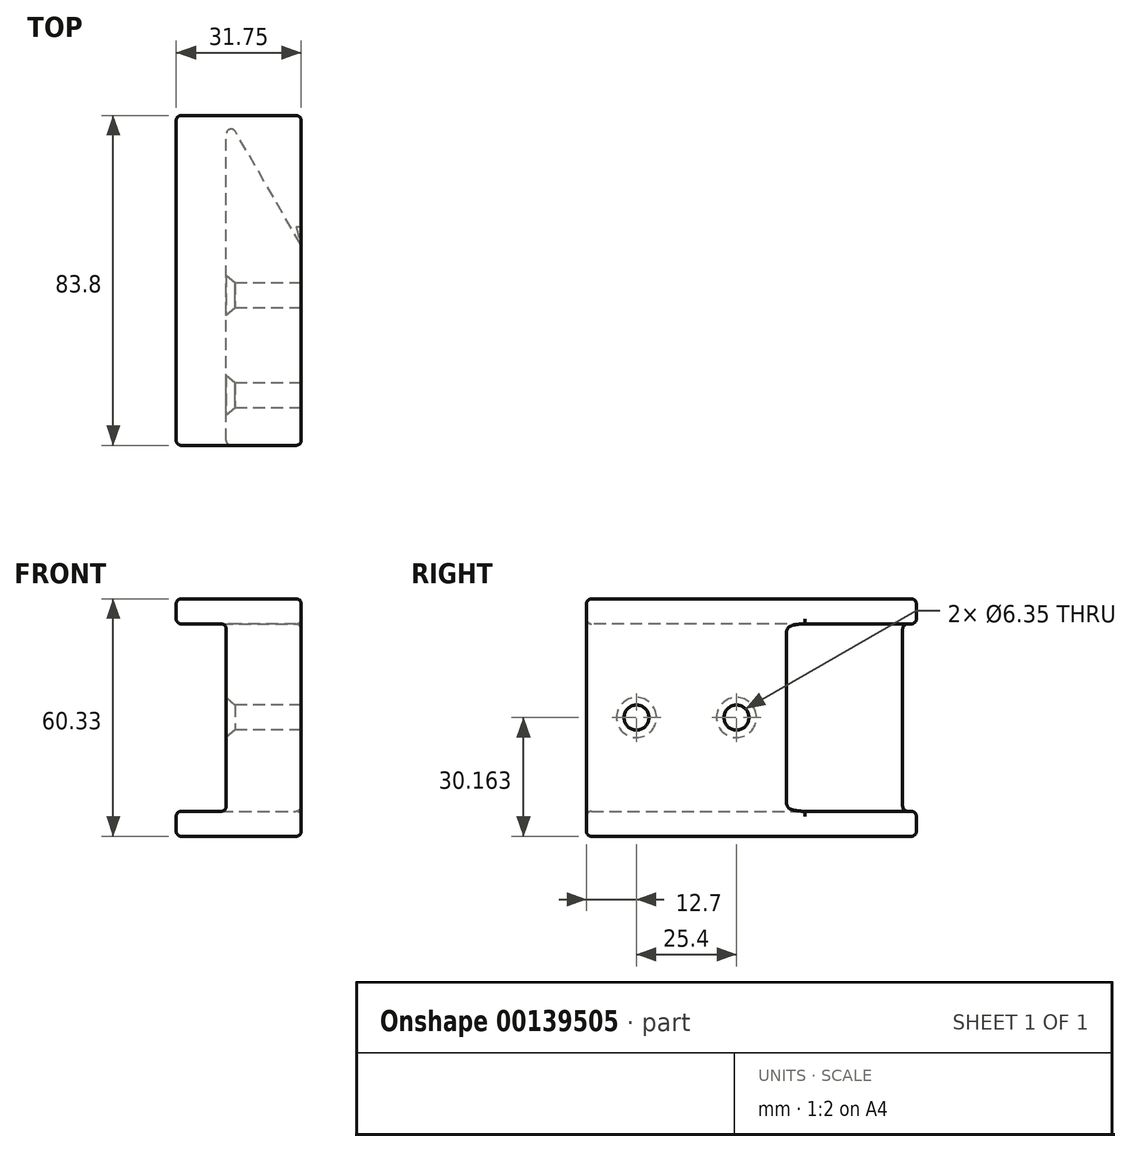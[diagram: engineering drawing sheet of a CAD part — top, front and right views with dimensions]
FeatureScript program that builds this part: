
annotation { "Feature Type Name" : "Feature", "Feature Type Description" : "" }
export const myFeature = defineFeature(function(context is Context, id is Id, definition is map)
    precondition{}
    {
        {
            var Q0;
            Q0=qCreatedBy(makeId("Top.planeOp"),FACE);
            var sketch = newSketch(context, id + "F0", { "sketchPlane" : qUnion([Q0])});
            skLineSegment(sketch, "E0", {"start": v(0, 0) * mm, "end": v(19.05, 0) * mm});
            skLineSegment(sketch, "E1", {"start": v(19.05, 0) * mm, "end": v(19.05, 50.8) * mm});
            skLineSegment(sketch, "E2", {"start": v(19.05, 50.8) * mm, "end": v(0, 83.8) * mm});
            skLineSegment(sketch, "E3", {"start": v(0, 83.8) * mm, "end": v(0, 0) * mm});
            skSolve(sketch);
        }
        {
            var Q0;
            Q0=makeQuery(id+"F0.imprint","IMPRINT",FACE,{"disambiguationData":[TD([[makeQuery(id+"F0.imprint","IMPRINT",EDGE,{"derivedFrom":sQuery(id+"F0.wireOp",EDGE,"E0")}),1.0]])]});
            extrude(context, id + "F1", {"entities" : qUnion([Q0]), "depth" : 60.32 * mm});
        }
        {
            var Q0;
            Q0=makeQuery(id+"F1.opExtrude","SWEPT_FACE",FACE,{"disambiguationData":[OSD([sQuery(id+"F0.wireOp",EDGE,"E3")])]});
            var sketch = newSketch(context, id + "F2", { "sketchPlane" : qUnion([Q0])});
            skPoint(sketch, "E4", {"position": v(-12.7, 30.16) * mm});
            skPoint(sketch, "E5", {"position": v(-38.1, 30.16) * mm});
            skLineSegment(sketch, "E6", {"start": v(-101.98, 30.16) * mm, "end": v(14.04, 30.16) * mm, "construction": true});
            skSolve(sketch);
        }
        {
            var Q0;
            Q0=sQuery(id+"F2.wireOp",VERTEX,"E4");
            var Q1;
            Q1=sQuery(id+"F2.wireOp",VERTEX,"E5");
            var Q2;
            Q2=sQuery(id+"F2.wireOp",VERTEX,"fd414b69-aa0b-4d1e-85eb-326c3dd4f586");
            var Q3;
            Q3=makeQuery(id+"F1.opExtrude","SWEPT_BODY",BODY,{"disambiguationData":[OSD([sQuery(id+"F0.wireOp",EDGE,"E0"),sQuery(id+"F0.wireOp",EDGE,"E1"),sQuery(id+"F0.wireOp",EDGE,"E2"),sQuery(id+"F0.wireOp",EDGE,"E3")])]});
            hole(context, id + "F3", {"style" : HoleStyle.C_SINK, "endStyle" : HoleEndStyle.THROUGH, "holeDiameter" : 6.35 * mm, "cSinkDiameter" : 10.16 * mm, "cSinkAngle" : 82 * degree, "startFromSketch" : true, "locations" : qUnion([Q0, Q1, Q2]), "scope" : qUnion([Q3]), "isTappedThrough" : true});
        }
        {
            var Q0;
            Q0=makeQuery(id+"F1.opExtrude","SWEPT_FACE",FACE,{"disambiguationData":[OSD([sQuery(id+"F0.wireOp",EDGE,"E1")])]});
            var sketch = newSketch(context, id + "F4", { "sketchPlane" : qUnion([Q0])});
            skLineSegment(sketch, "E7.bottom", {"start": v(83.8, 60.33) * mm, "end": v(0, 60.32) * mm});
            skLineSegment(sketch, "E7.top", {"start": v(83.8, 53.98) * mm, "end": v(0, 53.98) * mm});
            skLineSegment(sketch, "E7.left", {"start": v(83.8, 60.33) * mm, "end": v(83.8, 53.98) * mm});
            skLineSegment(sketch, "E7.right", {"start": v(0, 60.32) * mm, "end": v(0, 53.98) * mm});
            skLineSegment(sketch, "E8.bottom", {"start": v(0, 0) * mm, "end": v(83.8, 0) * mm});
            skLineSegment(sketch, "E8.top", {"start": v(0, 6.35) * mm, "end": v(83.8, 6.35) * mm});
            skLineSegment(sketch, "E8.left", {"start": v(0, 0) * mm, "end": v(0, 6.35) * mm});
            skLineSegment(sketch, "E8.right", {"start": v(83.8, 0) * mm, "end": v(83.8, 6.35) * mm});
            skSolve(sketch);
        }
        {
            var Q0;
            {var subQ3=sQuery(id+"F4.wireOp",EDGE,"E7.left");Q0=makeQuery(id+"F4.imprint","IMPRINT",FACE,{"disambiguationData":[TD([[makeQuery(id+"F4.imprint","IMPRINT",EDGE,{"derivedFrom":subQ3}),-1.0]])]});}
            var Q1;
            {var subQ3=sQuery(id+"F4.wireOp",EDGE,"E8.right");Q1=makeQuery(id+"F4.imprint","IMPRINT",FACE,{"disambiguationData":[TD([[makeQuery(id+"F4.imprint","IMPRINT",EDGE,{"derivedFrom":subQ3}),1.0]])]});}
            var Q2;
            {var subQ0=sQuery(id+"F4.wireOp",EDGE,"E7.right");Q2=makeQuery(id+"F4.imprint","IMPRINT",FACE,{"disambiguationData":[TD([[makeQuery(id+"F4.imprint","IMPRINT",EDGE,{"derivedFrom":subQ0}),1.0]])]});}
            var Q3;
            {var subQ0=sQuery(id+"F4.wireOp",EDGE,"E8.left");Q3=makeQuery(id+"F4.imprint","IMPRINT",FACE,{"disambiguationData":[TD([[makeQuery(id+"F4.imprint","IMPRINT",EDGE,{"derivedFrom":subQ0}),1.0]])]});}
            extrude(context, id + "F5", {"entities" : qUnion([Q0, Q1, Q2, Q3]), "operationType" : NewBodyOperationType.ADD, "oppositeDirection" : true, "depth" : 31.75 * mm});
        }
        {
            var Q0;
            Q0=makeQuery(id+"F5.opExtrude","CAP_EDGE",EDGE,{"disambiguationData":[OSD([sQuery(id+"F4.wireOp",EDGE,"E8.left")])],"isStart":false});
            var Q1;
            Q1=makeQuery(id+"F1.opExtrude","SWEPT_EDGE",EDGE,{"disambiguationData":[OSD([sQuery(id+"F0.wireOp",EDGE,"E0"),sQuery(id+"F0.wireOp",EDGE,"E1")])]});
            var Q2;
            Q2=makeQuery(id+"F5.opExtrude","CAP_EDGE",EDGE,{"disambiguationData":[OSD([sQuery(id+"F4.wireOp",EDGE,"E7.right")])],"isStart":false});
            var Q3;
            Q3=makeQuery(id+"F5.opExtrude","CAP_EDGE",EDGE,{"disambiguationData":[OSD([sQuery(id+"F4.wireOp",EDGE,"E7.left")])],"isStart":false});
            var Q4;
            Q4=makeQuery(id+"F5.opExtrude","CAP_EDGE",EDGE,{"disambiguationData":[OSD([sQuery(id+"F4.wireOp",EDGE,"E8.right")])],"isStart":false});
            var Q5;
            Q5=makeQuery(id+"F5.opExtrude","CAP_EDGE",EDGE,{"disambiguationData":[OSD([sQuery(id+"F4.wireOp",EDGE,"E8.right")])],"isStart":true});
            var Q6;
            Q6=makeQuery(id+"F5.opExtrude","CAP_EDGE",EDGE,{"disambiguationData":[OSD([sQuery(id+"F4.wireOp",EDGE,"E7.left")])],"isStart":true});
            fillet(context, id + "F6", {"entities" : qUnion([Q0, Q1, Q2, Q3, Q4, Q5, Q6]), "radius" : 1.27 * mm, "tangentPropagation" : true, "allowEdgeOverflow" : false});
        }
        {
            var Q0;
            Q0=makeQuery(id+"F5.opExtrude","SWEPT_EDGE",EDGE,{"disambiguationData":[OSD([sQuery(id+"F4.wireOp",EDGE,"E8.bottom"),sQuery(id+"F4.wireOp",EDGE,"E8.right")])]});
            var Q1;
            Q1=makeQuery(id+"F5.boolean.opBoolean","MERGE",FACE,{"derivedFrom":[makeQuery(id+"F1.opExtrude","CAP_FACE",FACE,{"disambiguationData":[OSD([sQuery(id+"F0.wireOp",EDGE,"E0"),sQuery(id+"F0.wireOp",EDGE,"E1"),sQuery(id+"F0.wireOp",EDGE,"E2"),sQuery(id+"F0.wireOp",EDGE,"E3")])],"isStart":false}),makeQuery(id+"F5.opExtrude","SWEPT_FACE",FACE,{"disambiguationData":[OSD([sQuery(id+"F4.wireOp",EDGE,"E7.bottom")])]})]});
            var Q2;
            Q2=makeQuery(id+"F1.opExtrude","SWEPT_EDGE",EDGE,{"disambiguationData":[OSD([sQuery(id+"F0.wireOp",EDGE,"E2"),sQuery(id+"F0.wireOp",EDGE,"E3")])]});
            fillet(context, id + "F7", {"entities" : qUnion([Q0, Q1, Q2]), "radius" : 1.27 * mm, "tangentPropagation" : true, "allowEdgeOverflow" : false});
        }
        {
            var Q0;
            Q0=makeQuery(id+"F5.opExtrude","CAP_EDGE",EDGE,{"disambiguationData":[OSD([sQuery(id+"F4.wireOp",EDGE,"E8.top")])],"isStart":true});
            var Q1;
            Q1=makeQuery(id+"F5.opExtrude","CAP_EDGE",EDGE,{"disambiguationData":[OSD([sQuery(id+"F4.wireOp",EDGE,"E7.top")])],"isStart":true});
            var Q2;
            Q2=makeQuery(id+"F1.opExtrude","SWEPT_EDGE",EDGE,{"disambiguationData":[OSD([sQuery(id+"F0.wireOp",EDGE,"E0"),sQuery(id+"F0.wireOp",EDGE,"E3")])]});
            var Q3;
            Q3=makeQuery(id+"F5.boolean.opBoolean","INTERSECT",EDGE,{"derivedFrom":[makeQuery(id+"F1.opExtrude","SWEPT_FACE",FACE,{"disambiguationData":[OSD([sQuery(id+"F0.wireOp",EDGE,"E3")])]}),makeQuery(id+"F5.opExtrude","SWEPT_FACE",FACE,{"disambiguationData":[OSD([sQuery(id+"F4.wireOp",EDGE,"E7.top")])]})]});
            var Q4;
            Q4=makeQuery(id+"F5.boolean.opBoolean","INTERSECT",EDGE,{"derivedFrom":[makeQuery(id+"F1.opExtrude","SWEPT_FACE",FACE,{"disambiguationData":[OSD([sQuery(id+"F0.wireOp",EDGE,"E3")])]}),makeQuery(id+"F5.opExtrude","SWEPT_FACE",FACE,{"disambiguationData":[OSD([sQuery(id+"F4.wireOp",EDGE,"E8.top")])]})]});
            fillet(context, id + "F8", {"entities" : qUnion([Q0, Q1, Q2, Q3, Q4]), "radius" : 1.27 * mm, "tangentPropagation" : true, "allowEdgeOverflow" : false});
        }
    });
